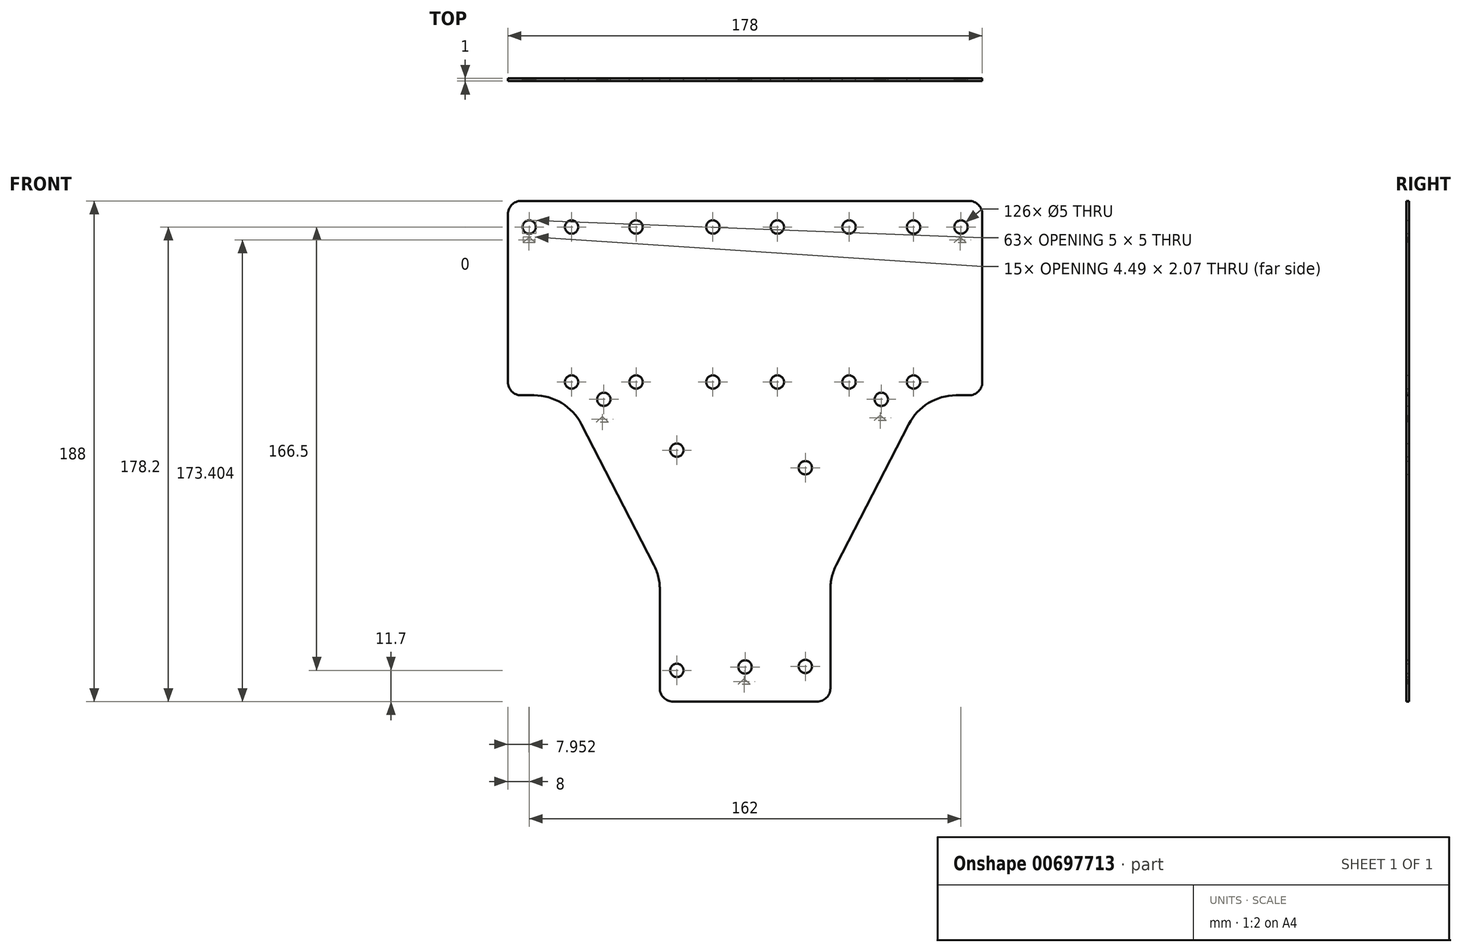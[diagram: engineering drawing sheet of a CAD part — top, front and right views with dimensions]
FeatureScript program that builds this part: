
annotation { "Feature Type Name" : "Feature", "Feature Type Description" : "" }
export const myFeature = defineFeature(function(context is Context, id is Id, definition is map)
    precondition{}
    {
        {
            var Q0;
            Q0=qCreatedBy(makeId("Front.planeOp"),FACE);
            var sketch = newSketch(context, id + "F0", { "sketchPlane" : qUnion([Q0])});
            skLineSegment(sketch, "E0.bottom", {"start": v(89, 83) * mm, "end": v(-89, 83) * mm});
            skLineSegment(sketch, "E0.top", {"start": v(89, -105) * mm, "end": v(-89, -105) * mm});
            skLineSegment(sketch, "E0.left", {"start": v(89, 83) * mm, "end": v(89, -105) * mm});
            skLineSegment(sketch, "E0.right", {"start": v(-89, 83) * mm, "end": v(-89, -105) * mm});
            skSolve(sketch);
        }
        {
            var Q0;
            Q0 = qSketchRegion(id + "F0", true);
            extrude(context, id + "F1", {"entities" : qUnion([Q0]), "depth" : 1 * mm, "offsetDistance" : 25 * mm});
        }
        {
            var Q0;
            Q0=makeQuery(id+"F1.opExtrude","CAP_FACE",FACE,{"disambiguationData":[OSD([sQuery(id+"F0.wireOp",EDGE,"E0.bottom"),sQuery(id+"F0.wireOp",EDGE,"E0.top"),sQuery(id+"F0.wireOp",EDGE,"E0.left"),sQuery(id+"F0.wireOp",EDGE,"E0.right")])],"isStart":true});
            var sketch = newSketch(context, id + "F2", { "sketchPlane" : qUnion([Q0])});
            skCircle(sketch, "E1", {"center": v(-81, 73.2) * mm, "radius": 2.5 * mm});
            skCircle(sketch, "E2", {"center": v(81, 73.2) * mm, "radius": 2.5 * mm});
            skCircle(sketch, "E3", {"center": v(53, 8.5) * mm, "radius": 2.5 * mm});
            skCircle(sketch, "E4", {"center": v(-51.1, 8.5) * mm, "radius": 2.5 * mm});
            skCircle(sketch, "E5", {"center": v(0, -92) * mm, "radius": 2.5 * mm});
            skCircle(sketch, "E6", {"center": v(-22.6, -91.8) * mm, "radius": 2.5 * mm});
            skCircle(sketch, "E7", {"center": v(25.6, -93.3) * mm, "radius": 2.5 * mm});
            skCircle(sketch, "E8", {"center": v(-22.6, -17.2) * mm, "radius": 2.5 * mm});
            skCircle(sketch, "E9", {"center": v(25.6, -10.6) * mm, "radius": 2.5 * mm});
            skCircle(sketch, "E10", {"center": v(-63.2, 73.2) * mm, "radius": 2.5 * mm});
            skCircle(sketch, "E11", {"center": v(-39, 73.2) * mm, "radius": 2.5 * mm});
            skCircle(sketch, "E12", {"center": v(-39, 15) * mm, "radius": 2.5 * mm});
            skCircle(sketch, "E13", {"center": v(-63.2, 15) * mm, "radius": 2.5 * mm});
            skCircle(sketch, "E14", {"center": v(40.9, 73.2) * mm, "radius": 2.5 * mm});
            skCircle(sketch, "E15", {"center": v(65.1, 73.2) * mm, "radius": 2.5 * mm});
            skCircle(sketch, "E16", {"center": v(65.1, 15) * mm, "radius": 2.5 * mm});
            skCircle(sketch, "E17", {"center": v(40.9, 15) * mm, "radius": 2.5 * mm});
            skCircle(sketch, "E18", {"center": v(-12.1, 73.2) * mm, "radius": 2.5 * mm});
            skCircle(sketch, "E19", {"center": v(12.1, 73.2) * mm, "radius": 2.5 * mm});
            skCircle(sketch, "E20", {"center": v(-12.1, 15) * mm, "radius": 2.5 * mm});
            skCircle(sketch, "E21", {"center": v(12.1, 15) * mm, "radius": 2.5 * mm});
            skSolve(sketch);
        }
        {
            var Q0;
            Q0 = qSketchRegion(id + "F2", true);
            extrude(context, id + "F3", {"entities" : qUnion([Q0]), "operationType" : NewBodyOperationType.REMOVE, "endBound" : BoundingType.THROUGH_ALL, "oppositeDirection" : true, "depth" : 25 * mm, "offsetDistance" : 25 * mm});
        }
        {
            var Q0;
            Q0=makeQuery(id+"F2.imprint","IMPRINT",FACE,{"disambiguationData":[TD([[makeQuery(id+"F2.imprint","IMPRINT",EDGE,{"derivedFrom":sQuery(id+"F2.wireOp",EDGE,"E1")}),-1.0]])]});
            var sketch = newSketch(context, id + "F4", { "sketchPlane" : qUnion([Q0])});
            skLineSegment(sketch, "E22", {"start": v(-32, -113) * mm, "end": v(-94, -113) * mm});
            skLineSegment(sketch, "E23", {"start": v(-94, -113) * mm, "end": v(-94, 10) * mm});
            skLineSegment(sketch, "E24", {"start": v(32, -113) * mm, "end": v(94, -113) * mm});
            skLineSegment(sketch, "E25", {"start": v(94, -113) * mm, "end": v(94, 10) * mm});
            skLineSegment(sketch, "E26", {"start": v(32, -58) * mm, "end": v(32, -113) * mm});
            skLineSegment(sketch, "E27", {"start": v(-32, -58) * mm, "end": v(-32, -113) * mm});
            skLineSegment(sketch, "E28", {"start": v(94, 10) * mm, "end": v(67, 10) * mm});
            skLineSegment(sketch, "E29", {"start": v(67, 10) * mm, "end": v(32, -58) * mm});
            skLineSegment(sketch, "E30", {"start": v(-94, 10) * mm, "end": v(-67, 10) * mm});
            skLineSegment(sketch, "E31", {"start": v(-67, 10) * mm, "end": v(-32, -58) * mm});
            skSolve(sketch);
        }
        {
            var Q0;
            Q0 = qSketchRegion(id + "F4", true);
            extrude(context, id + "F5", {"entities" : qUnion([Q0]), "operationType" : NewBodyOperationType.REMOVE, "endBound" : BoundingType.THROUGH_ALL, "oppositeDirection" : true, "depth" : 25 * mm, "offsetDistance" : 25 * mm});
        }
        {
            var Q0;
            Q0=makeQuery(id+"F1.opExtrude","SWEPT_EDGE",EDGE,{"disambiguationData":[OSD([sQuery(id+"F0.wireOp",EDGE,"E0.bottom"),sQuery(id+"F0.wireOp",EDGE,"E0.left")])]});
            var Q1;
            Q1=makeQuery(id+"F1.opExtrude","SWEPT_EDGE",EDGE,{"disambiguationData":[OSD([sQuery(id+"F0.wireOp",EDGE,"E0.bottom"),sQuery(id+"F0.wireOp",EDGE,"E0.right")])]});
            var Q2;
            Q2=makeQuery(id+"F5.boolean.opBoolean","INTERSECT",EDGE,{"derivedFrom":[makeQuery(id+"F1.opExtrude","SWEPT_FACE",FACE,{"disambiguationData":[OSD([sQuery(id+"F0.wireOp",EDGE,"E0.right")])]}),makeQuery(id+"F5.opExtrude","SWEPT_FACE",FACE,{"disambiguationData":[OSD([sQuery(id+"F4.wireOp",EDGE,"E28")])]})]});
            var Q3;
            Q3=makeQuery(id+"F5.boolean.opBoolean","INTERSECT",EDGE,{"derivedFrom":[makeQuery(id+"F1.opExtrude","SWEPT_FACE",FACE,{"disambiguationData":[OSD([sQuery(id+"F0.wireOp",EDGE,"E0.top")])]}),makeQuery(id+"F5.opExtrude","SWEPT_FACE",FACE,{"disambiguationData":[OSD([sQuery(id+"F4.wireOp",EDGE,"E26")])]})]});
            var Q4;
            Q4=makeQuery(id+"F5.boolean.opBoolean","INTERSECT",EDGE,{"derivedFrom":[makeQuery(id+"F1.opExtrude","SWEPT_FACE",FACE,{"disambiguationData":[OSD([sQuery(id+"F0.wireOp",EDGE,"E0.top")])]}),makeQuery(id+"F5.opExtrude","SWEPT_FACE",FACE,{"disambiguationData":[OSD([sQuery(id+"F4.wireOp",EDGE,"E27")])]})]});
            var Q5;
            Q5=makeQuery(id+"F5.boolean.opBoolean","INTERSECT",EDGE,{"derivedFrom":[makeQuery(id+"F1.opExtrude","SWEPT_FACE",FACE,{"disambiguationData":[OSD([sQuery(id+"F0.wireOp",EDGE,"E0.left")])]}),makeQuery(id+"F5.opExtrude","SWEPT_FACE",FACE,{"disambiguationData":[OSD([sQuery(id+"F4.wireOp",EDGE,"E30")])]})]});
            fillet(context, id + "F6", {"entities" : qUnion([Q0, Q1, Q2, Q3, Q4, Q5]), "radius" : 5 * mm, "tangentPropagation" : true, "allowEdgeOverflow" : false});
        }
        {
            var Q0;
            Q0=makeQuery(id+"F5.boolean.opBoolean","COPY",EDGE,{"derivedFrom":makeQuery(id+"F5.opExtrude","SWEPT_EDGE",EDGE,{"disambiguationData":[OSD([sQuery(id+"F4.wireOp",EDGE,"E30"),sQuery(id+"F4.wireOp",EDGE,"E31")])]})});
            var Q1;
            Q1=makeQuery(id+"F5.boolean.opBoolean","COPY",EDGE,{"derivedFrom":makeQuery(id+"F5.opExtrude","SWEPT_EDGE",EDGE,{"disambiguationData":[OSD([sQuery(id+"F4.wireOp",EDGE,"E27"),sQuery(id+"F4.wireOp",EDGE,"E31")])]})});
            var Q2;
            Q2=makeQuery(id+"F5.boolean.opBoolean","COPY",EDGE,{"derivedFrom":makeQuery(id+"F5.opExtrude","SWEPT_EDGE",EDGE,{"disambiguationData":[OSD([sQuery(id+"F4.wireOp",EDGE,"E26"),sQuery(id+"F4.wireOp",EDGE,"E29")])]})});
            var Q3;
            Q3=makeQuery(id+"F5.boolean.opBoolean","COPY",EDGE,{"derivedFrom":makeQuery(id+"F5.opExtrude","SWEPT_EDGE",EDGE,{"disambiguationData":[OSD([sQuery(id+"F4.wireOp",EDGE,"E28"),sQuery(id+"F4.wireOp",EDGE,"E29")])]})});
            fillet(context, id + "F7", {"entities" : qUnion([Q0, Q1, Q2, Q3]), "radius" : 20 * mm, "tangentPropagation" : true, "allowEdgeOverflow" : false});
        }
        {
            var Q0;
            Q0=makeQuery(id+"F0.imprint","IMPRINT",FACE,{"disambiguationData":[TD([[makeQuery(id+"F0.imprint","IMPRINT",EDGE,{"derivedFrom":sQuery(id+"F0.wireOp",EDGE,"E0.bottom")}),1.0]])]});
            var sketch = newSketch(context, id + "F8", { "sketchPlane" : qUnion([Q0])});
            skLineSegment(sketch, "E32", {"start": v(80.66, 69.43) * mm, "end": v(82.95, 67.37) * mm});
            skLineSegment(sketch, "E33", {"start": v(82.95, 67.37) * mm, "end": v(78.45, 67.37) * mm});
            skLineSegment(sketch, "E34", {"start": v(78.45, 67.37) * mm, "end": v(80.66, 69.43) * mm});
            skLineSegment(sketch, "E35", {"start": v(50.69, 2.6) * mm, "end": v(52.97, 0.53) * mm});
            skLineSegment(sketch, "E36", {"start": v(52.97, 0.53) * mm, "end": v(48.48, 0.53) * mm});
            skLineSegment(sketch, "E37", {"start": v(48.48, 0.53) * mm, "end": v(50.69, 2.6) * mm});
            skLineSegment(sketch, "E38", {"start": v(-53.59, 2) * mm, "end": v(-51.3, -0.06) * mm});
            skLineSegment(sketch, "E39", {"start": v(-51.3, -0.06) * mm, "end": v(-55.8, -0.06) * mm});
            skLineSegment(sketch, "E40", {"start": v(-55.8, -0.06) * mm, "end": v(-53.59, 2) * mm});
            skLineSegment(sketch, "E41", {"start": v(-0.4, -96.45) * mm, "end": v(1.9, -98.52) * mm});
            skLineSegment(sketch, "E42", {"start": v(1.9, -98.52) * mm, "end": v(-2.6, -98.52) * mm});
            skLineSegment(sketch, "E43", {"start": v(-2.6, -98.52) * mm, "end": v(-0.4, -96.45) * mm});
            skLineSegment(sketch, "E44", {"start": v(-81.09, 69.44) * mm, "end": v(-78.8, 67.37) * mm});
            skLineSegment(sketch, "E45", {"start": v(-78.8, 67.37) * mm, "end": v(-83.3, 67.37) * mm});
            skLineSegment(sketch, "E46", {"start": v(-83.3, 67.37) * mm, "end": v(-81.09, 69.44) * mm});
            skSolve(sketch);
        }
        {
            var Q0;
            Q0 = qSketchRegion(id + "F8", true);
            extrude(context, id + "F9", {"entities" : qUnion([Q0]), "operationType" : NewBodyOperationType.REMOVE, "depth" : 0.3 * mm, "offsetDistance" : 25 * mm});
        }
    });
